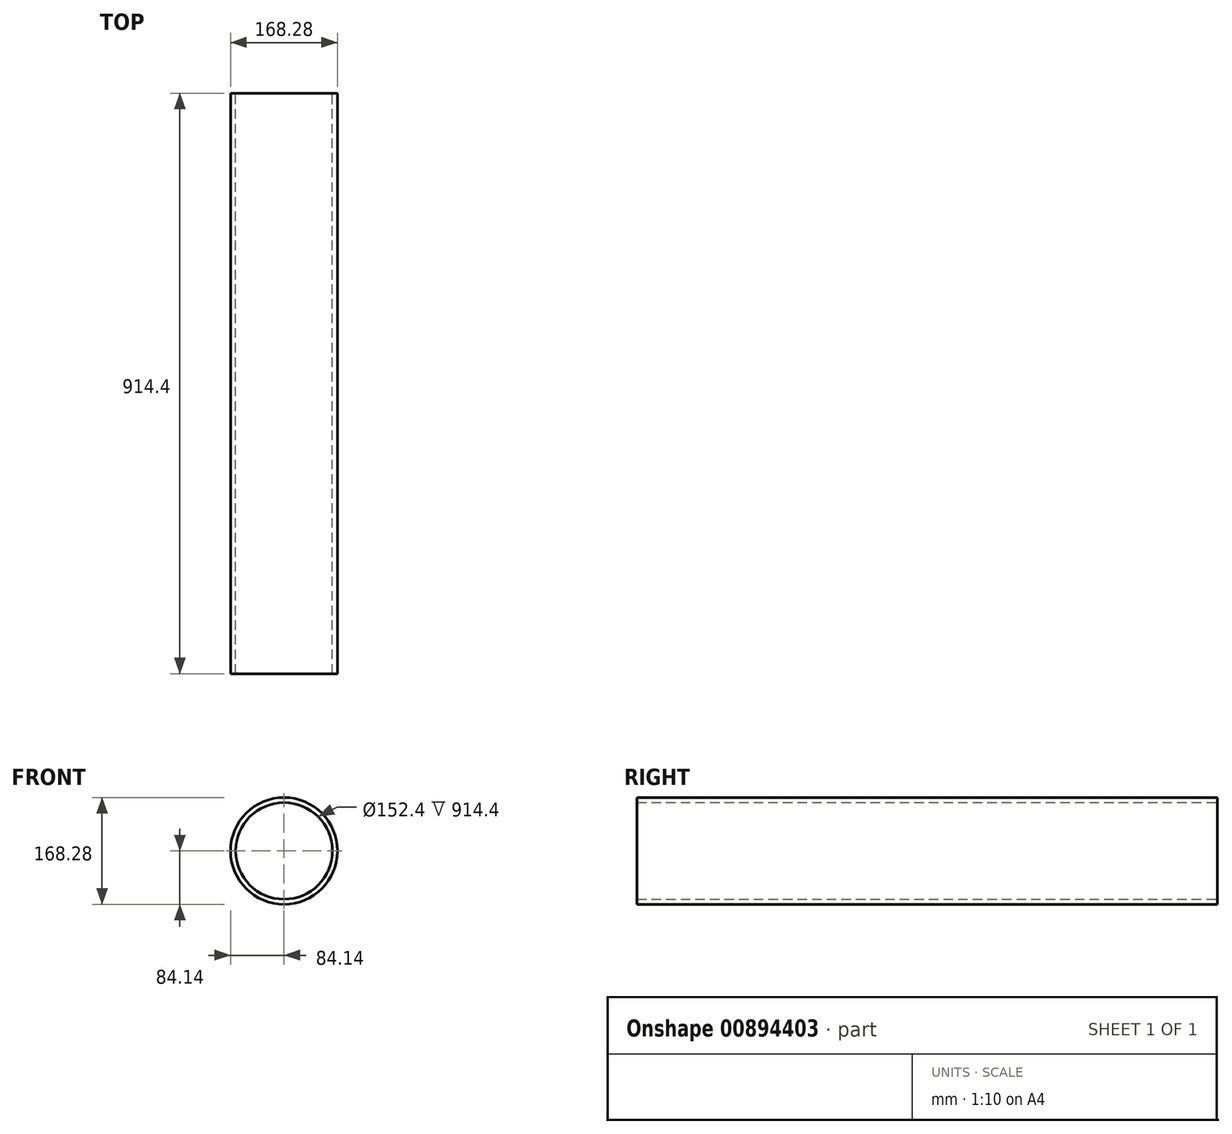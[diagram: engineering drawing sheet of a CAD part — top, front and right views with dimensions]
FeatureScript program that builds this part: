
annotation { "Feature Type Name" : "Feature", "Feature Type Description" : "" }
export const myFeature = defineFeature(function(context is Context, id is Id, definition is map)
    precondition{}
    {
        {
            var Q0;
            Q0=qCreatedBy(makeId("Front.planeOp"),FACE);
            var sketch = newSketch(context, id + "F0", { "sketchPlane" : qUnion([Q0])});
            skCircle(sketch, "E0", {"center": v(0, 0) * mm, "radius": 84.14 * mm});
            skCircle(sketch, "E1", {"center": v(0, 0) * mm, "radius": 76.2 * mm});
            skSolve(sketch);
        }
        {
            var Q0;
            Q0 = qSketchRegion(id + "F0", true);
            extrude(context, id + "F1", {"entities" : qUnion([Q0]), "depth" : 914.4 * mm, "offsetDistance" : 25.4 * mm});
        }
    });
